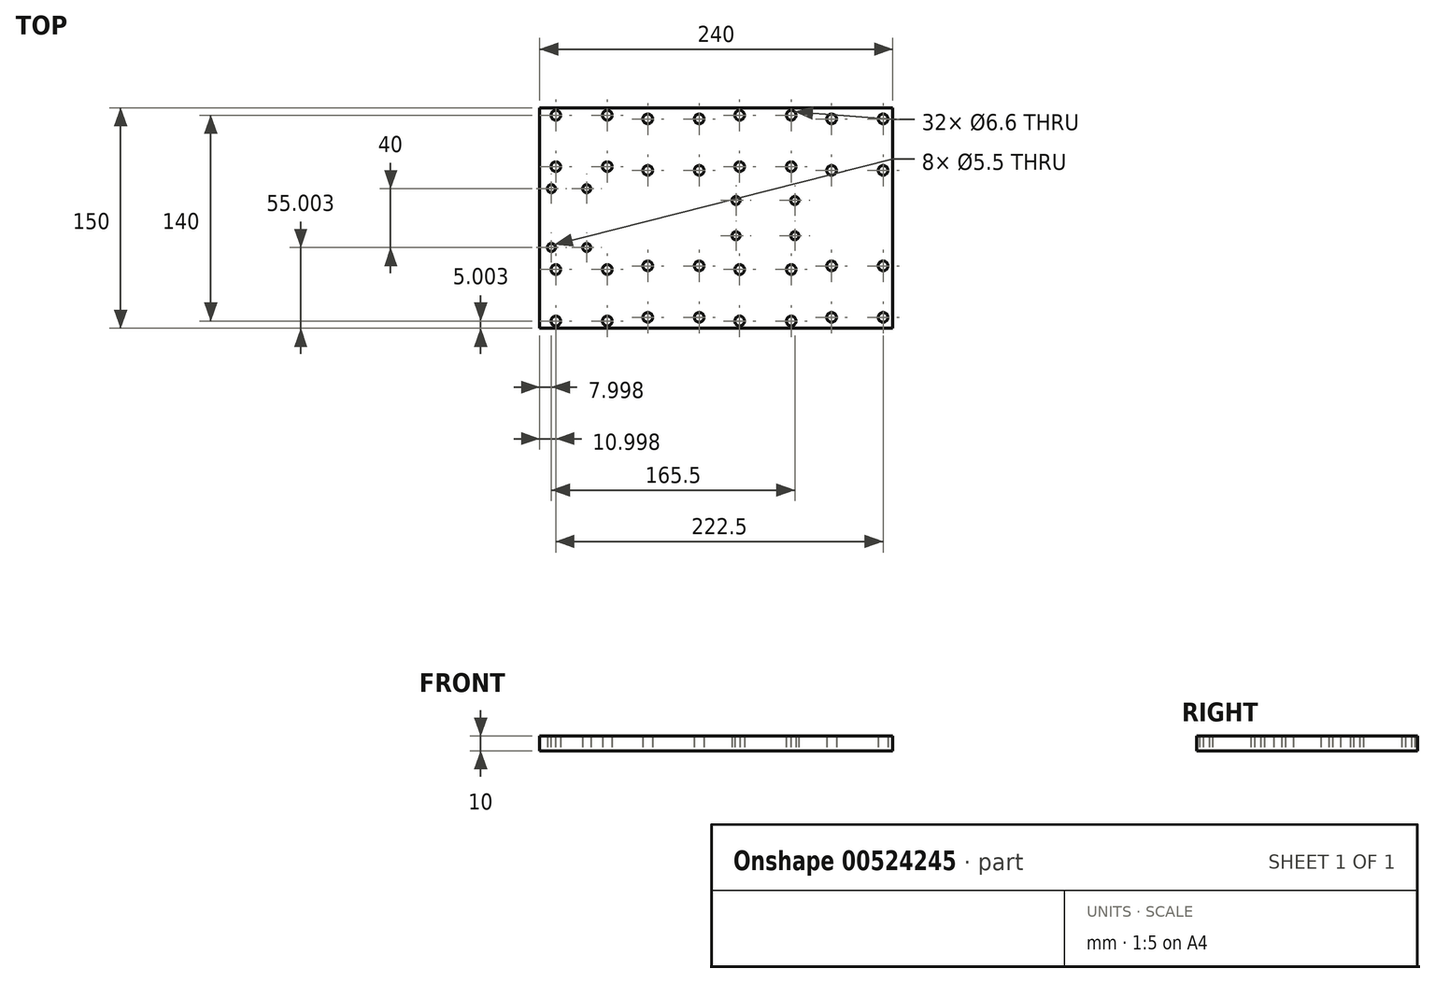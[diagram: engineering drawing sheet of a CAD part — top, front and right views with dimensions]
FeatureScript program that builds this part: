
annotation { "Feature Type Name" : "Feature", "Feature Type Description" : "" }
export const myFeature = defineFeature(function(context is Context, id is Id, definition is map)
    precondition{}
    {
        {
            var Q0;
            Q0=qCreatedBy(makeId("Top.planeOp"),FACE);
            var sketch = newSketch(context, id + "F0", { "sketchPlane" : qUnion([Q0])});
            skLineSegment(sketch, "E0.bottom", {"start": v(123.89, -72.44) * mm, "end": v(-116.11, -72.44) * mm});
            skLineSegment(sketch, "E0.top", {"start": v(123.89, 77.56) * mm, "end": v(-116.11, 77.56) * mm});
            skLineSegment(sketch, "E0.left", {"start": v(123.89, -72.44) * mm, "end": v(123.89, 77.56) * mm});
            skLineSegment(sketch, "E0.right", {"start": v(-116.11, -72.44) * mm, "end": v(-116.11, 77.56) * mm});
            skPoint(sketch, "E1", {"position": v(117.39, 70.06) * mm});
            skPoint(sketch, "E2", {"position": v(82.39, 70.06) * mm});
            skPoint(sketch, "E3", {"position": v(82.39, 35.06) * mm});
            skPoint(sketch, "E4", {"position": v(117.39, 35.06) * mm});
            skPoint(sketch, "E5", {"position": v(117.39, -29.94) * mm});
            skPoint(sketch, "E6", {"position": v(82.39, -29.94) * mm});
            skPoint(sketch, "E7", {"position": v(82.39, -64.94) * mm});
            skPoint(sketch, "E8", {"position": v(117.39, -64.94) * mm});
            skPoint(sketch, "E9", {"position": v(-7.61, 70.06) * mm});
            skPoint(sketch, "E10", {"position": v(-42.61, 70.06) * mm});
            skPoint(sketch, "E11", {"position": v(-42.61, 35.06) * mm});
            skPoint(sketch, "E12", {"position": v(-7.61, 35.06) * mm});
            skPoint(sketch, "E13", {"position": v(-7.61, -29.94) * mm});
            skPoint(sketch, "E14", {"position": v(-42.61, -29.94) * mm});
            skPoint(sketch, "E15", {"position": v(-42.61, -64.94) * mm});
            skPoint(sketch, "E16", {"position": v(-7.61, -64.94) * mm});
            skPoint(sketch, "E17", {"position": v(19.89, -32.44) * mm});
            skPoint(sketch, "E18", {"position": v(54.89, -32.44) * mm});
            skPoint(sketch, "E19", {"position": v(19.89, -67.44) * mm});
            skPoint(sketch, "E20", {"position": v(54.89, -67.44) * mm});
            skPoint(sketch, "E21", {"position": v(19.89, 72.56) * mm});
            skPoint(sketch, "E22", {"position": v(54.89, 72.56) * mm});
            skPoint(sketch, "E23", {"position": v(19.89, 37.56) * mm});
            skPoint(sketch, "E24", {"position": v(54.89, 37.56) * mm});
            skPoint(sketch, "E25", {"position": v(-105.11, -32.44) * mm});
            skPoint(sketch, "E26", {"position": v(-70.11, -32.44) * mm});
            skPoint(sketch, "E27", {"position": v(-105.11, -67.44) * mm});
            skPoint(sketch, "E28", {"position": v(-70.11, -67.44) * mm});
            skPoint(sketch, "E29", {"position": v(-105.11, 72.56) * mm});
            skPoint(sketch, "E30", {"position": v(-70.11, 72.56) * mm});
            skPoint(sketch, "E31", {"position": v(-105.11, 37.56) * mm});
            skPoint(sketch, "E32", {"position": v(-70.11, 37.56) * mm});
            skPoint(sketch, "E33", {"position": v(17.39, 14.56) * mm});
            skPoint(sketch, "E34", {"position": v(57.39, 14.56) * mm});
            skPoint(sketch, "E35", {"position": v(17.39, -9.44) * mm});
            skPoint(sketch, "E36", {"position": v(57.39, -9.44) * mm});
            skPoint(sketch, "E37", {"position": v(-108.11, 22.56) * mm});
            skPoint(sketch, "E38", {"position": v(-84.11, 22.56) * mm});
            skPoint(sketch, "E39", {"position": v(-108.11, -17.44) * mm});
            skPoint(sketch, "E40", {"position": v(-84.11, -17.44) * mm});
            skSolve(sketch);
        }
        {
            var Q0;
            Q0 = qSketchRegion(id + "F0", true);
            extrude(context, id + "F1", {"entities" : qUnion([Q0]), "depth" : 10 * mm, "offsetDistance" : 25 * mm});
        }
        {
            var Q0;
            Q0=sQuery(id+"F0.wireOp",VERTEX,"E13");
            var Q1;
            Q1=sQuery(id+"F0.wireOp",VERTEX,"E11");
            var Q2;
            Q2=sQuery(id+"F0.wireOp",VERTEX,"E14");
            var Q3;
            Q3=sQuery(id+"F0.wireOp",VERTEX,"E15");
            var Q4;
            Q4=sQuery(id+"F0.wireOp",VERTEX,"E12");
            var Q5;
            Q5=sQuery(id+"F0.wireOp",VERTEX,"E10");
            var Q6;
            Q6=sQuery(id+"F0.wireOp",VERTEX,"E3");
            var Q7;
            Q7=sQuery(id+"F0.wireOp",VERTEX,"E9");
            var Q8;
            Q8=sQuery(id+"F0.wireOp",VERTEX,"E6");
            var Q9;
            Q9=sQuery(id+"F0.wireOp",VERTEX,"E7");
            var Q10;
            Q10=sQuery(id+"F0.wireOp",VERTEX,"E5");
            var Q11;
            Q11=sQuery(id+"F0.wireOp",VERTEX,"E4");
            var Q12;
            Q12=sQuery(id+"F0.wireOp",VERTEX,"E2");
            var Q13;
            Q13=sQuery(id+"F0.wireOp",VERTEX,"E1");
            var Q14;
            Q14=sQuery(id+"F0.wireOp",VERTEX,"E8");
            var Q15;
            Q15=sQuery(id+"F0.wireOp",VERTEX,"E16");
            var Q16;
            Q16=makeQuery(id+"F1.opExtrude","SWEPT_BODY",BODY,{"disambiguationData":[OSD([sQuery(id+"F0.wireOp",EDGE,"E0.bottom"),sQuery(id+"F0.wireOp",EDGE,"E0.top"),sQuery(id+"F0.wireOp",EDGE,"E0.left"),sQuery(id+"F0.wireOp",EDGE,"E0.right")])]});
            hole(context, id + "F2", {"style" : HoleStyle.SIMPLE, "endStyle" : HoleEndStyle.THROUGH, "oppositeDirection" : true, "standardTappedOrClearance" : lookupTablePath({ "standard" : "ISO", "fit" : "Normal", "size" : "M6", "type" : "Clearance" }), "standardBlindInLast" : lookupTablePath({ "fit" : "Standard", "standard" : "ISO", "size" : "M6", "type" : "Clearance" }), "holeDiameter" : 6.6 * mm, "isTappedThrough" : true, "tappedDepth" : 12 * mm, "tapClearance" : 3, "locations" : qUnion([Q0, Q1, Q2, Q3, Q4, Q5, Q6, Q7, Q8, Q9, Q10, Q11, Q12, Q13, Q14, Q15]), "scope" : qUnion([Q16])});
        }
        {
            var Q0;
            Q0=sQuery(id+"F0.wireOp",VERTEX,"E26");
            var Q1;
            Q1=sQuery(id+"F0.wireOp",VERTEX,"E28");
            var Q2;
            Q2=sQuery(id+"F0.wireOp",VERTEX,"E30");
            var Q3;
            Q3=sQuery(id+"F0.wireOp",VERTEX,"E31");
            var Q4;
            Q4=sQuery(id+"F0.wireOp",VERTEX,"E29");
            var Q5;
            Q5=sQuery(id+"F0.wireOp",VERTEX,"E27");
            var Q6;
            Q6=sQuery(id+"F0.wireOp",VERTEX,"E25");
            var Q7;
            Q7=sQuery(id+"F0.wireOp",VERTEX,"E32");
            var Q8;
            Q8=sQuery(id+"F0.wireOp",VERTEX,"E21");
            var Q9;
            Q9=sQuery(id+"F0.wireOp",VERTEX,"E22");
            var Q10;
            Q10=sQuery(id+"F0.wireOp",VERTEX,"E24");
            var Q11;
            Q11=sQuery(id+"F0.wireOp",VERTEX,"E23");
            var Q12;
            Q12=sQuery(id+"F0.wireOp",VERTEX,"E18");
            var Q13;
            Q13=sQuery(id+"F0.wireOp",VERTEX,"E19");
            var Q14;
            Q14=sQuery(id+"F0.wireOp",VERTEX,"E20");
            var Q15;
            Q15=sQuery(id+"F0.wireOp",VERTEX,"E17");
            var Q16;
            Q16=makeQuery(id+"F1.opExtrude","SWEPT_BODY",BODY,{"disambiguationData":[OSD([sQuery(id+"F0.wireOp",EDGE,"E0.bottom"),sQuery(id+"F0.wireOp",EDGE,"E0.top"),sQuery(id+"F0.wireOp",EDGE,"E0.left"),sQuery(id+"F0.wireOp",EDGE,"E0.right")])]});
            hole(context, id + "F3", {"style" : HoleStyle.SIMPLE, "endStyle" : HoleEndStyle.THROUGH, "oppositeDirection" : true, "standardTappedOrClearance" : lookupTablePath({ "standard" : "ISO", "fit" : "Normal", "size" : "M6", "type" : "Clearance" }), "standardBlindInLast" : lookupTablePath({ "fit" : "Standard", "standard" : "ISO", "size" : "M6", "type" : "Clearance" }), "holeDiameter" : 6.6 * mm, "isTappedThrough" : true, "tappedDepth" : 12 * mm, "tapClearance" : 3, "locations" : qUnion([Q0, Q1, Q2, Q3, Q4, Q5, Q6, Q7, Q8, Q9, Q10, Q11, Q12, Q13, Q14, Q15]), "scope" : qUnion([Q16])});
        }
        {
            var Q0;
            Q0=sQuery(id+"F0.wireOp",VERTEX,"E33");
            var Q1;
            Q1=sQuery(id+"F0.wireOp",VERTEX,"E35");
            var Q2;
            Q2=sQuery(id+"F0.wireOp",VERTEX,"E36");
            var Q3;
            Q3=sQuery(id+"F0.wireOp",VERTEX,"E34");
            var Q4;
            Q4=makeQuery(id+"F1.opExtrude","SWEPT_BODY",BODY,{"disambiguationData":[OSD([sQuery(id+"F0.wireOp",EDGE,"E0.bottom"),sQuery(id+"F0.wireOp",EDGE,"E0.top"),sQuery(id+"F0.wireOp",EDGE,"E0.left"),sQuery(id+"F0.wireOp",EDGE,"E0.right")])]});
            hole(context, id + "F4", {"style" : HoleStyle.SIMPLE, "endStyle" : HoleEndStyle.THROUGH, "oppositeDirection" : true, "standardTappedOrClearance" : lookupTablePath({ "standard" : "ISO", "fit" : "Normal", "size" : "M5", "type" : "Clearance" }), "standardBlindInLast" : lookupTablePath({ "fit" : "Standard", "standard" : "ISO", "size" : "M5", "type" : "Clearance" }), "holeDiameter" : 5.5 * mm, "isTappedThrough" : true, "tappedDepth" : 12 * mm, "tapClearance" : 3, "locations" : qUnion([Q0, Q1, Q2, Q3]), "scope" : qUnion([Q4])});
        }
        {
            var Q0;
            Q0=sQuery(id+"F0.wireOp",VERTEX,"E37");
            var Q1;
            Q1=sQuery(id+"F0.wireOp",VERTEX,"E38");
            var Q2;
            Q2=sQuery(id+"F0.wireOp",VERTEX,"E39");
            var Q3;
            Q3=sQuery(id+"F0.wireOp",VERTEX,"E40");
            var Q4;
            Q4=makeQuery(id+"F1.opExtrude","SWEPT_BODY",BODY,{"disambiguationData":[OSD([sQuery(id+"F0.wireOp",EDGE,"E0.bottom"),sQuery(id+"F0.wireOp",EDGE,"E0.top"),sQuery(id+"F0.wireOp",EDGE,"E0.left"),sQuery(id+"F0.wireOp",EDGE,"E0.right")])]});
            hole(context, id + "F5", {"style" : HoleStyle.SIMPLE, "endStyle" : HoleEndStyle.THROUGH, "oppositeDirection" : true, "standardTappedOrClearance" : lookupTablePath({ "standard" : "ISO", "fit" : "Normal", "size" : "M5", "type" : "Clearance" }), "standardBlindInLast" : lookupTablePath({ "fit" : "Standard", "standard" : "ISO", "size" : "M5", "type" : "Clearance" }), "holeDiameter" : 5.5 * mm, "isTappedThrough" : true, "tappedDepth" : 12 * mm, "tapClearance" : 3, "locations" : qUnion([Q0, Q1, Q2, Q3]), "scope" : qUnion([Q4])});
        }
    });
